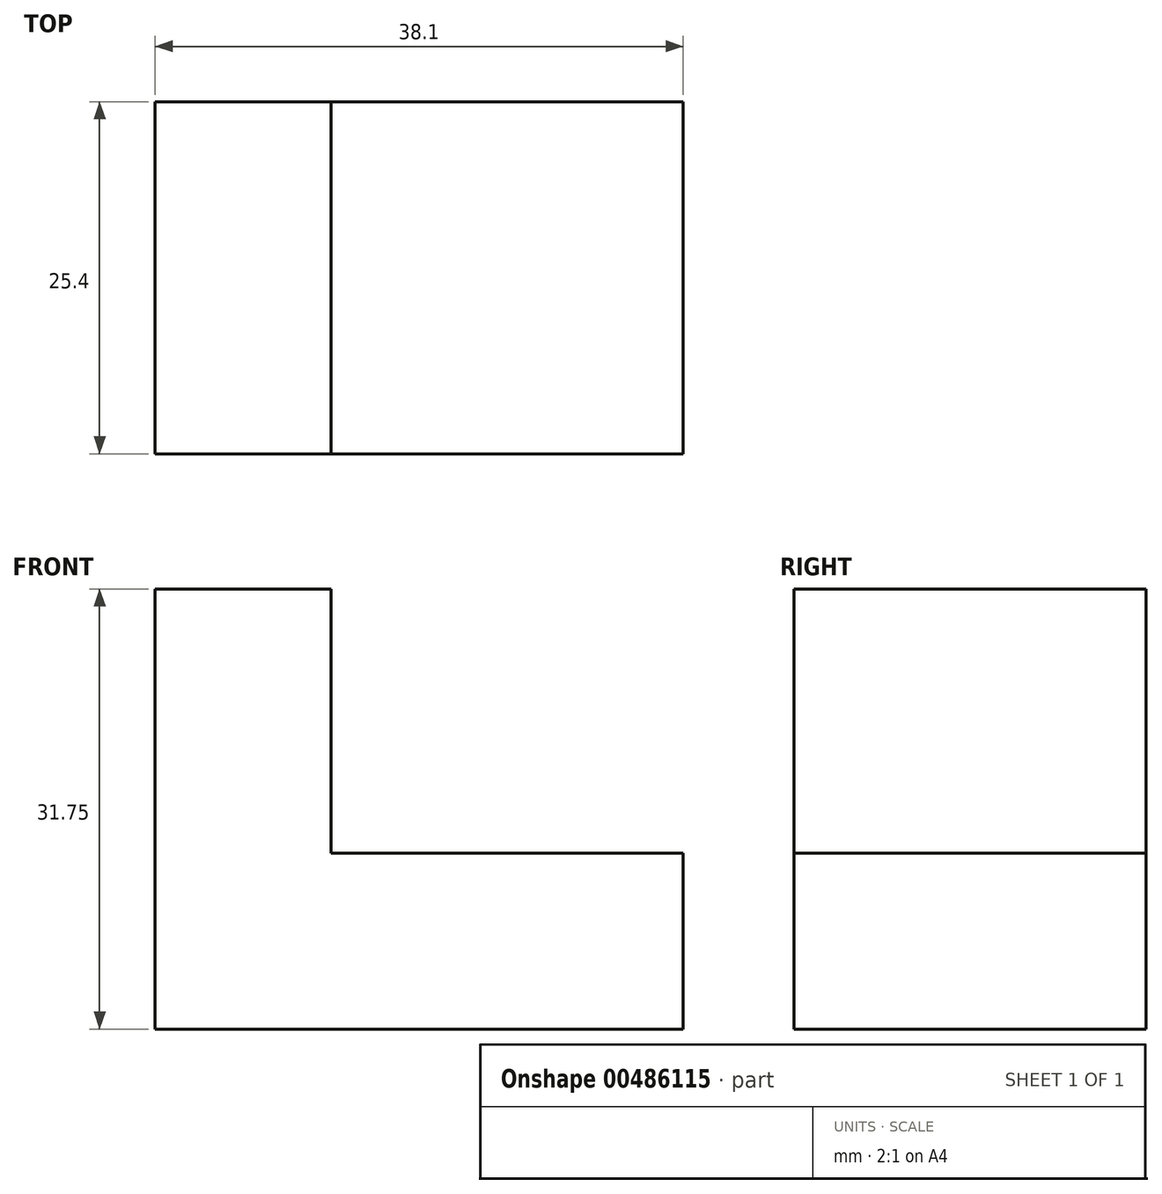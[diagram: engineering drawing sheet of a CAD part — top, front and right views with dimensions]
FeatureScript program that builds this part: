
annotation { "Feature Type Name" : "Feature", "Feature Type Description" : "" }
export const myFeature = defineFeature(function(context is Context, id is Id, definition is map)
    precondition{}
    {
        {
            var Q0;
            Q0=qCreatedBy(makeId("Front.planeOp"),FACE);
            var sketch = newSketch(context, id + "F0", { "sketchPlane" : qUnion([Q0])});
            skLineSegment(sketch, "E0", {"start": v(-50.51, 11.78) * mm, "end": v(-12.41, 11.78) * mm});
            skLineSegment(sketch, "E1", {"start": v(-12.41, 11.78) * mm, "end": v(-12.41, 24.48) * mm});
            skLineSegment(sketch, "E2", {"start": v(-12.41, 24.48) * mm, "end": v(-37.81, 24.48) * mm});
            skLineSegment(sketch, "E3", {"start": v(-37.81, 24.48) * mm, "end": v(-37.81, 43.53) * mm});
            skLineSegment(sketch, "E4", {"start": v(-37.81, 43.53) * mm, "end": v(-50.51, 43.53) * mm});
            skLineSegment(sketch, "E5", {"start": v(-50.51, 43.53) * mm, "end": v(-50.51, 11.78) * mm});
            skSolve(sketch);
        }
        {
            var Q0;
            Q0=makeQuery(id+"F0.imprint","IMPRINT",FACE,{"disambiguationData":[TD([[makeQuery(id+"F0.imprint","IMPRINT",EDGE,{"derivedFrom":sQuery(id+"F0.wireOp",EDGE,"E0")}),1.0]])]});
            extrude(context, id + "F1", {"entities" : qUnion([Q0]), "depth" : 25.4 * mm, "offsetDistance" : 25.4 * mm});
        }
    });
